# Revit family: DoubleTBeamSegment
name_source: partatom
category: Structural Framing
units: mm (PartAtom-declared; Revit-internal decimal feet)

## family parameters
Always export as geometry = No
Always vertical = Yes
Cut with Voids When Loaded = No
Display in Hidden Views = Edges Hidden by Other Members
Material for Model Behavior = Concrete
OmniClass Number = 23.25.30.11.14.14
OmniClass Title = Beams
Section Shape = User Defined
Shared = Yes
Show family pre-cut in plan views = Yes

## types (1)
- DoubleTBeamSegment
    Sofistik Section Left = $ Revit defined Cross Section
SECT 1 BTYP 'BEAM' TITL 'T_Section_left' MNO 1 MRF 2
$ Polygonal Shape
POLY TYPE O
VERT NO Y               Z
VERT 1  =-#Lane         0
VERT 2  =-#Lane         =#Slab_Height
VERT 3  =-#Beam_Width/2 =#Slab_Height
VERT 4  =-#Beam_Width/2 '=#Beam_Height'
VERT 5  =#Beam_Width/2  '=#Beam_Height'
VERT 6  =#Beam_Width/2  =#Slab_Height
VERT 7  =#Parapet       =#Parapet_Height
VERT 8  =#Parapet       0
    Sofistik Section Right = $ Revit defined Cross Section
SECT 2 BTYP 'BEAM' TITL 'T_Section_right' MNO 1 MRF 2
$ Polygonal Shape
POLY TYPE O
VERT NO Y               Z
VERT 1  =#Lane          0
VERT 2  =#Lane          =#Slab_Height
VERT 3  =#Beam_Width/2  =#Slab_Height
VERT 4  =#Beam_Width/2  '=#Beam_Height'
VERT 5  =-#Beam_Width/2 '=#Beam_Height'
VERT 6  =-#Beam_Width/2 =#Slab_Height
VERT 7  =-#Parapet      =#Parapet_Height
VERT 8  =-#Parapet      0

## geometry (parser evidence)
native form markers: Sweep x5
no freeform markers — native parametric forms only
